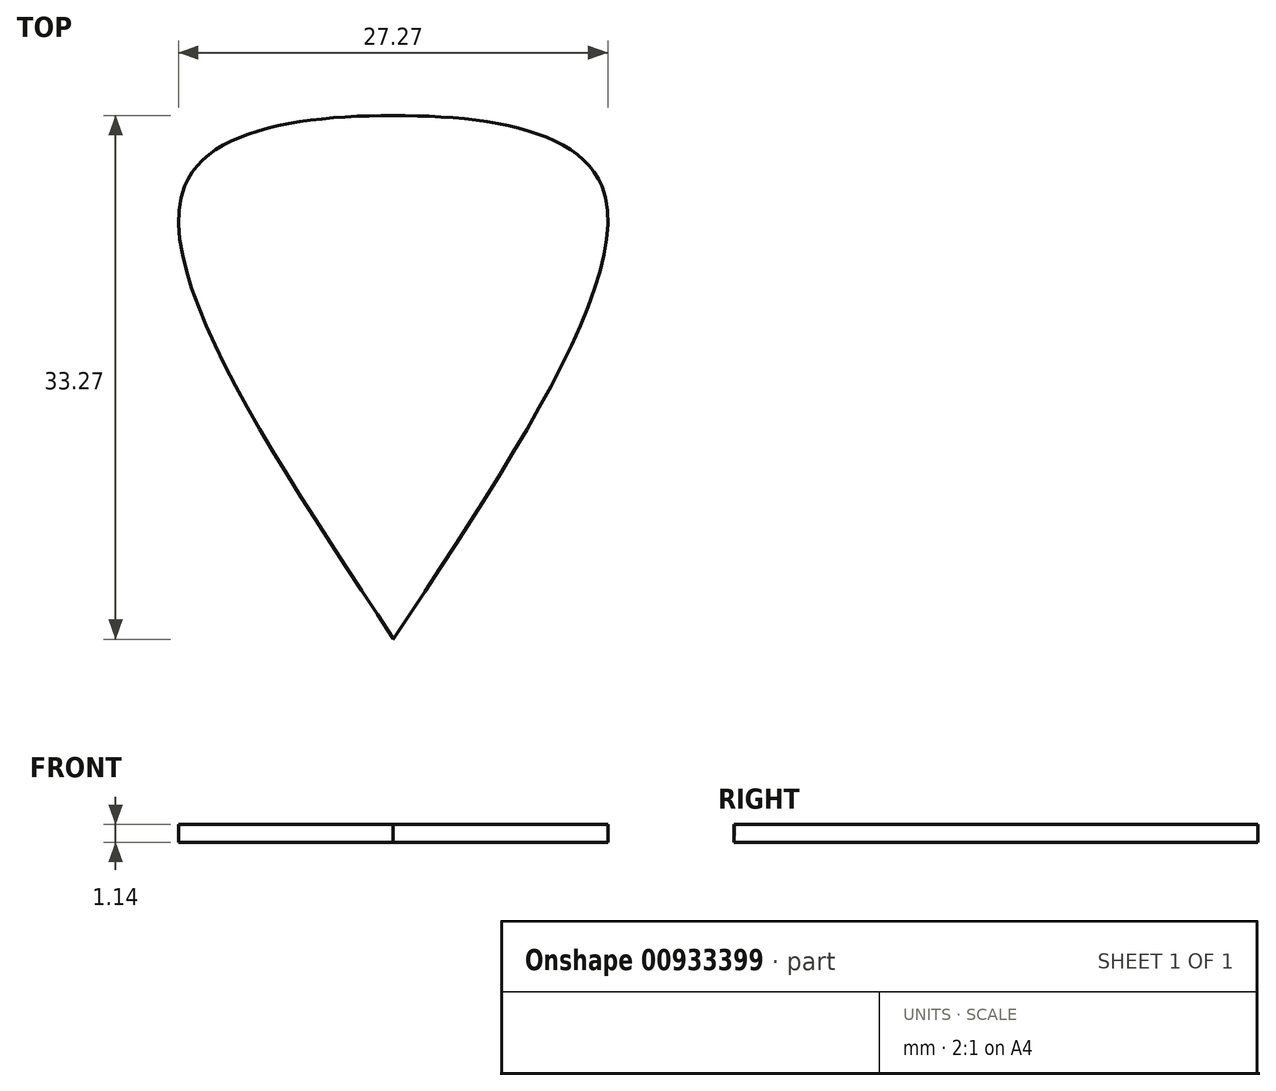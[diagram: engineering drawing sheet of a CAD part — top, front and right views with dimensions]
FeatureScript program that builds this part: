
annotation { "Feature Type Name" : "Feature", "Feature Type Description" : "" }
export const myFeature = defineFeature(function(context is Context, id is Id, definition is map)
    precondition{}
    {
        {
            var Q0;
            Q0=qCreatedBy(makeId("Top.planeOp"), FACE);
            var sketch = newSketch(context, id + "F0", { "sketchPlane" : qUnion([Q0])});
            skLineSegment(sketch, "E0", {"start": v(-31.75, 26.37) * mm, "end": v(-5.26, 26.37) * mm});
            skLineSegment(sketch, "E1", {"start": v(-18.5, 26.37) * mm, "end": v(-18.5, -2.43) * mm});
            skLineSegment(sketch, "E2", {"start": v(-18.5, 26.37) * mm, "end": v(-18.5, 30.84) * mm});
            skFitSpline(sketch, "E3", {"points": [v(-18.5, -2.43) * mm, v(-5.26, 26.37) * mm, v(-18.5, 30.84) * mm, v(-31.75, 26.37) * mm, v(-18.5, -2.36) * mm], "startDerivative": vector(77.26, 116.56) * mm, "endDerivative": vector(77.3, -116.39) * mm});
            skCircle(sketch, "E4", {"center": v(-25.56, 26.96) * mm, "radius": 0.65 * mm, "construction": true});
            skCircle(sketch, "E5", {"center": v(-23.43, 27.07) * mm, "radius": 0.66 * mm, "construction": true});
            skCircle(sketch, "E6", {"center": v(-21.84, 27.1) * mm, "radius": 0.66 * mm, "construction": true});
            skCircle(sketch, "E7", {"center": v(-19.53, 27.22) * mm, "radius": 0.66 * mm, "construction": true});
            skCircle(sketch, "E8", {"center": v(-18.01, 27.15) * mm, "radius": 0.66 * mm, "construction": true});
            skCircle(sketch, "E9", {"center": v(-16.2, 27.18) * mm, "radius": 0.66 * mm, "construction": true});
            skCircle(sketch, "E10", {"center": v(-14.3, 27.15) * mm, "radius": 0.66 * mm, "construction": true});
            skCircle(sketch, "E11", {"center": v(-12.06, 27.22) * mm, "radius": 0.66 * mm, "construction": true});
            skCircle(sketch, "E12", {"center": v(-24.99, 25.25) * mm, "radius": 0.66 * mm, "construction": true});
            skCircle(sketch, "E13", {"center": v(-25.82, 23.89) * mm, "radius": 0.66 * mm, "construction": true});
            skCircle(sketch, "E14", {"center": v(-22.07, 24.83) * mm, "radius": 0.66 * mm, "construction": true});
            skCircle(sketch, "E15", {"center": v(-24.12, 23.77) * mm, "radius": 0.66 * mm, "construction": true});
            skCircle(sketch, "E16", {"center": v(-20.1, 25.36) * mm, "radius": 0.66 * mm, "construction": true});
            skCircle(sketch, "E17", {"center": v(-20.55, 23.54) * mm, "radius": 0.66 * mm, "construction": true});
            skCircle(sketch, "E18", {"center": v(-23.5, 25.86) * mm, "radius": 0.66 * mm, "construction": true});
            skCircle(sketch, "E19", {"center": v(-17.06, 25.4) * mm, "radius": 0.66 * mm, "construction": true});
            skCircle(sketch, "E20", {"center": v(-18.8, 24.23) * mm, "radius": 0.66 * mm, "construction": true});
            skCircle(sketch, "E21", {"center": v(-16.76, 23.47) * mm, "radius": 0.66 * mm, "construction": true});
            skCircle(sketch, "E22", {"center": v(-15.02, 25.25) * mm, "radius": 0.66 * mm, "construction": true});
            skCircle(sketch, "E23", {"center": v(-11.75, 25.67) * mm, "radius": 0.66 * mm, "construction": true});
            skCircle(sketch, "E24", {"center": v(-13.46, 23.96) * mm, "radius": 0.66 * mm, "construction": true});
            skCircle(sketch, "E25", {"center": v(-13.42, 25.74) * mm, "radius": 0.66 * mm, "construction": true});
            skCircle(sketch, "E26", {"center": v(-15.05, 23.47) * mm, "radius": 0.66 * mm, "construction": true});
            skCircle(sketch, "E27", {"center": v(-11.11, 23.58) * mm, "radius": 0.66 * mm, "construction": true});
            skCircle(sketch, "E28", {"center": v(-10.62, 27.22) * mm, "radius": 0.66 * mm, "construction": true});
            skCircle(sketch, "E29", {"center": v(-22.3, 23.4) * mm, "radius": 0.66 * mm, "construction": true});
            skCircle(sketch, "E30", {"center": v(-18.58, 25.78) * mm, "radius": 0.66 * mm, "construction": true});
            skSolve(sketch);
        }
        {
            var Q0;
            Q0 = qSketchRegion(id + "F0", true);
            extrude(context, id + "F1", {"entities" : qUnion([Q0]), "depth" : 1.14 * mm, "offsetDistance" : 25.4 * mm});
        }
    });
